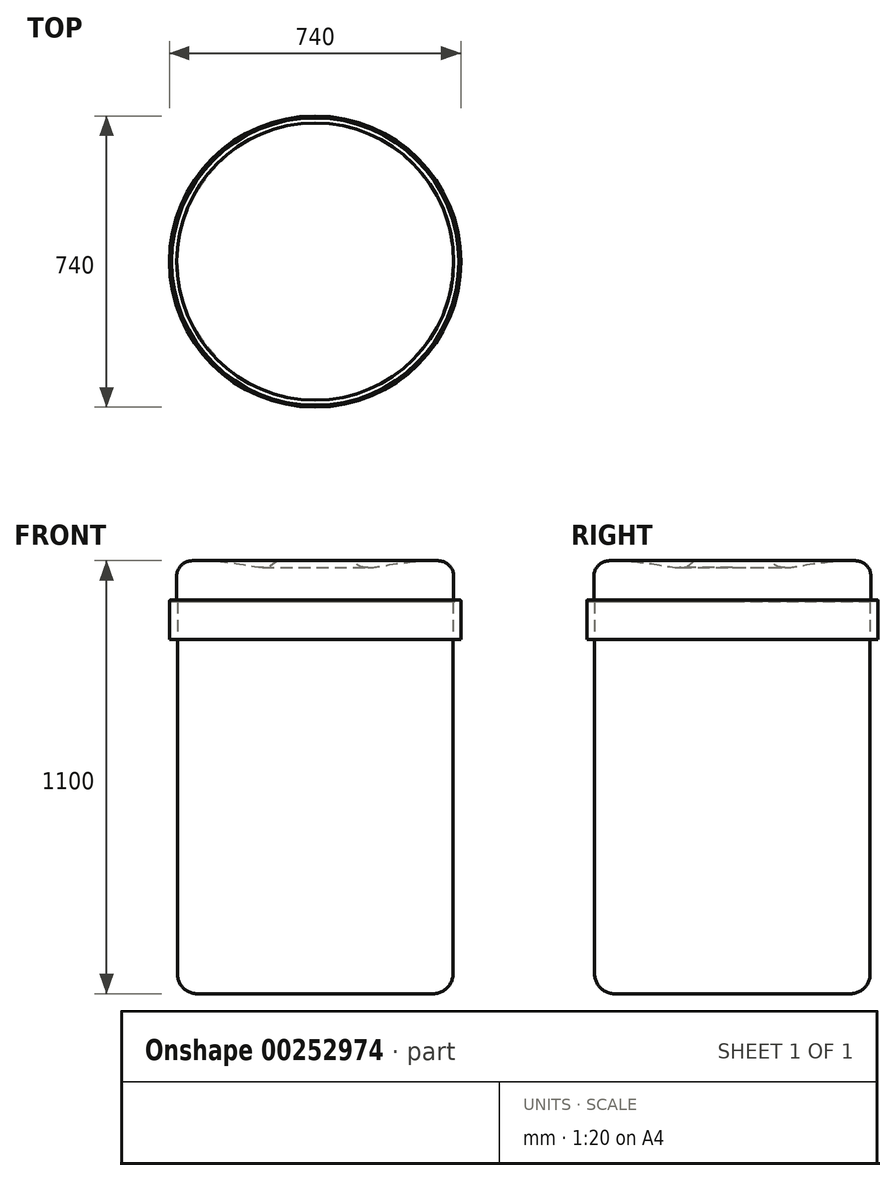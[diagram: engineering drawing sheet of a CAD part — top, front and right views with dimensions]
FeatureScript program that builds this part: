
annotation { "Feature Type Name" : "Feature", "Feature Type Description" : "" }
export const myFeature = defineFeature(function(context is Context, id is Id, definition is map)
    precondition{}
    {
        {
            var Q0;
            Q0=qCreatedBy(makeId("Front.planeOp"),FACE);
            var sketch = newSketch(context, id + "F0", { "sketchPlane" : qUnion([Q0])});
            skLineSegment(sketch, "E0", {"start": v(350, 0) * mm, "end": v(350, -950) * mm});
            skLineSegment(sketch, "E1", {"start": v(300, -1000) * mm, "end": v(0, -1000) * mm});
            skLineSegment(sketch, "E2", {"start": v(0, -1127.56) * mm, "end": v(0, 0) * mm, "construction": true});
            skLineSegment(sketch, "E3", {"start": v(350, 0) * mm, "end": v(0, 0) * mm});
            skLineSegment(sketch, "E4", {"start": v(0, -1000) * mm, "end": v(0, 0) * mm});
            skPoint(sketch, "E5.visualSharp", {"position": v(350, -1000) * mm});
            skArc(sketch, "E5.filletArc", {"start": v(300, -1000) * mm, "mid": v(335.36, -985.36) * mm, "end": v(350, -950) * mm});
            skSolve(sketch);
        }
        {
            var Q0;
            Q0=qSketchRegion(id+"F0",true);
            var Q1;
            Q1=sQuery(id+"F0.wireOp",EDGE,"E2");
            revolve(context, id + "F1", {"entities" : qUnion([Q0]), "axis" : qUnion([Q1]), "revolveType" : RevolveType.FULL});
        }
        {
            var Q0;
            Q0=qCreatedBy(makeId("Front.planeOp"),FACE);
            var sketch = newSketch(context, id + "F2", { "sketchPlane" : qUnion([Q0])});
            skLineSegment(sketch, "E6", {"start": v(350, 0) * mm, "end": v(350, -950) * mm, "construction": true});
            skLineSegment(sketch, "E7.bottom", {"start": v(350, 0) * mm, "end": v(365, 0) * mm});
            skLineSegment(sketch, "E7.top", {"start": v(350, -4) * mm, "end": v(365, -4) * mm});
            skLineSegment(sketch, "E7.left", {"start": v(350, 0) * mm, "end": v(350, -4) * mm});
            skLineSegment(sketch, "E7.right", {"start": v(365, 0) * mm, "end": v(365, -4) * mm});
            skSolve(sketch);
        }
        {
            var Q0;
            Q0=qSketchRegion(id+"F2",true);
            var Q1;
            Q1=sQuery(id+"F0.wireOp",EDGE,"E4");
            revolve(context, id + "F3", {"operationType" : NewBodyOperationType.ADD, "entities" : qUnion([Q0]), "axis" : qUnion([Q1]), "revolveType" : RevolveType.FULL});
        }
        {
            var Q0;
            Q0=qCreatedBy(makeId("Front.planeOp"),FACE);
            var sketch = newSketch(context, id + "F4", { "sketchPlane" : qUnion([Q0])});
            skLineSegment(sketch, "E8", {"start": v(354, 0) * mm, "end": v(368, 0) * mm});
            skLineSegment(sketch, "E9", {"start": v(370, -2) * mm, "end": v(370, -100) * mm});
            skLineSegment(sketch, "E10", {"start": v(370, -100) * mm, "end": v(0, -100) * mm});
            skLineSegment(sketch, "E11", {"start": v(0, -100) * mm, "end": v(0, 100) * mm});
            skLineSegment(sketch, "E12", {"start": v(0, 100) * mm, "end": v(352, 100) * mm, "construction": true});
            skLineSegment(sketch, "E13", {"start": v(352, 60) * mm, "end": v(352, 2) * mm});
            skFitSpline(sketch, "E14", {"points": [v(90, 100) * mm, v(110.21, 88.12) * mm, v(137.65, 82.48) * mm, v(181.42, 88.59) * mm, v(230.39, 95.55) * mm, v(302, 100) * mm], "startDerivative": vector(189.51, 0.06) * mm, "endDerivative": vector(395.3, 0) * mm});
            skLineSegment(sketch, "E15", {"start": v(90, 100) * mm, "end": v(0, 100) * mm});
            skLineSegment(sketch, "E16", {"start": v(302, 100) * mm, "end": v(312, 100) * mm});
            skPoint(sketch, "E17.visualSharp", {"position": v(352, 100) * mm});
            skArc(sketch, "E17.filletArc", {"start": v(352, 60) * mm, "mid": v(340.28, 88.28) * mm, "end": v(312, 100) * mm});
            skPoint(sketch, "E18.visualSharp", {"position": v(370, 0) * mm});
            skArc(sketch, "E18.filletArc", {"start": v(370, -2) * mm, "mid": v(369.41, -0.59) * mm, "end": v(368, 0) * mm});
            skPoint(sketch, "E19.visualSharp", {"position": v(352, 0) * mm});
            skArc(sketch, "E19.filletArc", {"start": v(352, 2) * mm, "mid": v(352.59, 0.59) * mm, "end": v(354, 0) * mm});
            skSolve(sketch);
        }
        {
            var Q0;
            Q0=makeQuery(id+"F4.imprint","IMPRINT",FACE,{"disambiguationData":[TD([[makeQuery(id+"F4.imprint","IMPRINT",EDGE,{"derivedFrom":sQuery(id+"F4.wireOp",EDGE,"E8")}),-1.0]])]});
            var Q1;
            Q1=sQuery(id+"F4.wireOp",EDGE,"E11");
            revolve(context, id + "F5", {"entities" : qUnion([Q0]), "axis" : qUnion([Q1]), "revolveType" : RevolveType.FULL});
        }
    });
